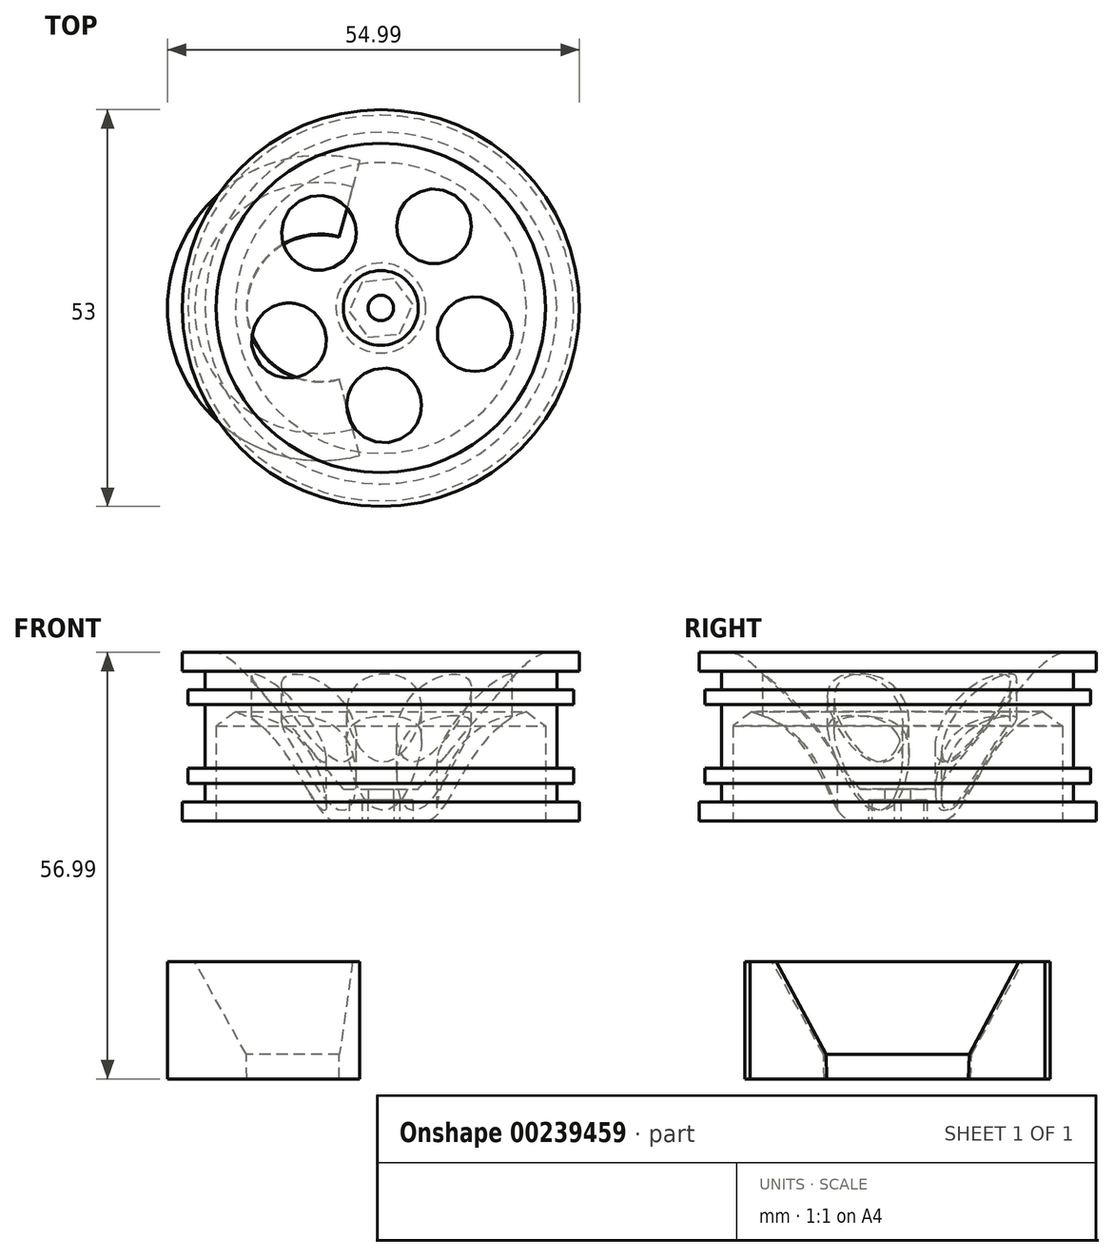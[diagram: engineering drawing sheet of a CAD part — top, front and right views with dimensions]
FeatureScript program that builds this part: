
annotation { "Feature Type Name" : "Feature", "Feature Type Description" : "" }
export const myFeature = defineFeature(function(context is Context, id is Id, definition is map)
    precondition{}
    {
        {
            var Q0;
            Q0=qCreatedBy(makeId("Front.planeOp"),FACE);
            var sketch = newSketch(context, id + "F0", { "sketchPlane" : qUnion([Q0])});
            skLineSegment(sketch, "E0", {"start": v(-30.1, -5.77) * mm, "end": v(-34.6, -5.77) * mm});
            skLineSegment(sketch, "E1", {"start": v(-34.6, -5.77) * mm, "end": v(-34.6, -8.27) * mm});
            skLineSegment(sketch, "E2", {"start": v(-34.6, -8.27) * mm, "end": v(-31.6, -8.27) * mm});
            skLineSegment(sketch, "E3", {"start": v(-31.6, -8.27) * mm, "end": v(-31.6, -10.77) * mm});
            skLineSegment(sketch, "E4", {"start": v(-31.6, -10.77) * mm, "end": v(-33.84, -10.77) * mm});
            skLineSegment(sketch, "E5", {"start": v(-33.84, -10.77) * mm, "end": v(-33.84, -12.77) * mm});
            skLineSegment(sketch, "E6", {"start": v(-33.84, -12.77) * mm, "end": v(-31.6, -12.77) * mm});
            skLineSegment(sketch, "E7", {"start": v(-31.6, -12.77) * mm, "end": v(-31.6, -21.27) * mm});
            skLineSegment(sketch, "E8", {"start": v(-31.6, -21.27) * mm, "end": v(-33.84, -21.27) * mm});
            skLineSegment(sketch, "E9", {"start": v(-33.84, -21.27) * mm, "end": v(-33.84, -23.27) * mm});
            skLineSegment(sketch, "E10", {"start": v(-33.84, -23.27) * mm, "end": v(-31.6, -23.27) * mm});
            skLineSegment(sketch, "E11", {"start": v(-31.6, -23.27) * mm, "end": v(-31.6, -25.77) * mm});
            skLineSegment(sketch, "E12", {"start": v(-31.6, -25.77) * mm, "end": v(-34.6, -25.77) * mm});
            skLineSegment(sketch, "E13", {"start": v(-34.6, -25.77) * mm, "end": v(-34.6, -28.27) * mm});
            skLineSegment(sketch, "E14", {"start": v(-34.6, -28.27) * mm, "end": v(-30.1, -28.27) * mm});
            skLineSegment(sketch, "E15", {"start": v(-14.1, -28.27) * mm, "end": v(-9.8, -28.27) * mm});
            skLineSegment(sketch, "E16", {"start": v(-9.8, -28.27) * mm, "end": v(-9.8, -24.02) * mm});
            skLineSegment(sketch, "E17", {"start": v(-9.8, -24.02) * mm, "end": v(-13.1, -24.02) * mm});
            skLineSegment(sketch, "E18", {"start": v(-9.8, -28.27) * mm, "end": v(-8.1, -28.27) * mm});
            skLineSegment(sketch, "E19", {"start": v(-8.1, -28.27) * mm, "end": v(-8.1, -24.02) * mm});
            skLineSegment(sketch, "E20", {"start": v(-8.1, -24.02) * mm, "end": v(-9.8, -24.02) * mm});
            skLineSegment(sketch, "E21", {"start": v(-30.1, -28.27) * mm, "end": v(-30.1, -15.63) * mm});
            skFitSpline(sketch, "E22", {"points": [v(-30.1, -13.27) * mm, v(-25.48, -14.59) * mm, v(-19.31, -21.6) * mm, v(-14.1, -28.27) * mm], "startDerivative": vector(14.77, -0.8) * mm, "endDerivative": vector(13.28, 1.86) * mm});
            skLineSegment(sketch, "E23", {"start": v(-30.1, -15.63) * mm, "end": v(-27.52, -13.71) * mm});
            skFitSpline(sketch, "E24", {"points": [v(-13.1, -24.02) * mm, v(-16.9, -19.47) * mm, v(-23.9, -11.2) * mm, v(-30.1, -5.77) * mm], "startDerivative": vector(-12.08, 13.61) * mm, "endDerivative": vector(-19.93, 6.13) * mm});
            skSolve(sketch);
        }
        {
            var Q0;
            Q0=makeQuery(id+"F0.imprint","IMPRINT",FACE,{"disambiguationData":[TD([[makeQuery(id+"F0.imprint","IMPRINT",EDGE,{"derivedFrom":sQuery(id+"F0.wireOp",EDGE,"E0")}),1.0]])]});
            var Q1;
            Q1=sQuery(id+"F0.wireOp",EDGE,"E19");
            revolve(context, id + "F1", {"entities" : qUnion([Q0]), "axis" : qUnion([Q1]), "revolveType" : RevolveType.FULL});
        }
        {
            var Q0;
            Q0=makeQuery(id+"F1.opRevolve","SWEPT_BODY",BODY,{"disambiguationData":[OSD([sQuery(id+"F0.wireOp",EDGE,"E0"),sQuery(id+"F0.wireOp",EDGE,"E1"),sQuery(id+"F0.wireOp",EDGE,"E2"),sQuery(id+"F0.wireOp",EDGE,"E3"),sQuery(id+"F0.wireOp",EDGE,"E4"),sQuery(id+"F0.wireOp",EDGE,"E5"),sQuery(id+"F0.wireOp",EDGE,"E6"),sQuery(id+"F0.wireOp",EDGE,"E7"),sQuery(id+"F0.wireOp",EDGE,"E8"),sQuery(id+"F0.wireOp",EDGE,"E9"),sQuery(id+"F0.wireOp",EDGE,"E10"),sQuery(id+"F0.wireOp",EDGE,"E11"),sQuery(id+"F0.wireOp",EDGE,"E12"),sQuery(id+"F0.wireOp",EDGE,"E13"),sQuery(id+"F0.wireOp",EDGE,"E14"),sQuery(id+"F0.wireOp",EDGE,"E15"),sQuery(id+"F0.wireOp",EDGE,"E16"),sQuery(id+"F0.wireOp",EDGE,"E17"),sQuery(id+"F0.wireOp",EDGE,"d1fe35fa-0e64-46eb-b905-4f6e5b59d955"),sQuery(id+"F0.wireOp",EDGE,"E21"),sQuery(id+"F0.wireOp",EDGE,"E22"),sQuery(id+"F0.wireOp",EDGE,"128adb2e-220a-4990-bb0a-539939f27e0b.filletArc")])]});
            transform(context, id + "F2", {"entities" : qUnion([Q0]), "transformType" : TransformType.TRANSLATION_3D, "dx" : 8.1 * mm, "dy" : 0 * mm, "dz" : 0 * mm, "makeCopy" : false});
        }
        {
            var Q0;
            Q0=qCreatedBy(makeId("Top.planeOp"),FACE);
            var sketch = newSketch(context, id + "F3", { "sketchPlane" : qUnion([Q0])});
            skCircle(sketch, "E25", {"center": v(-8.27, 10.04) * mm, "radius": 5 * mm});
            skCircle(sketch, "E26.1.0", {"center": v(7.1, 10.9) * mm, "radius": 5 * mm});
            skCircle(sketch, "E26.2.0", {"center": v(12.53, -3.49) * mm, "radius": 5 * mm});
            skCircle(sketch, "E26.3.0", {"center": v(0.44, -13) * mm, "radius": 5 * mm});
            skCircle(sketch, "E26.4.0", {"center": v(-12.27, -4.33) * mm, "radius": 5 * mm});
            skPoint(sketch, "E26.center", {"position": v(0, 0) * mm});
            skLineSegment(sketch, "E26.anchor1", {"start": v(0, 0) * mm, "end": v(-8.27, 10.04) * mm, "construction": true});
            skLineSegment(sketch, "E26.anchor2", {"start": v(0, 0) * mm, "end": v(-12.27, -4.33) * mm, "construction": true});
            skSolve(sketch);
        }
        {
            var Q0;
            Q0=makeQuery(id+"F3.imprint","IMPRINT",FACE,{"disambiguationData":[TD([[makeQuery(id+"F3.imprint","IMPRINT",EDGE,{"derivedFrom":sQuery(id+"F3.wireOp",EDGE,"E25")}),1.0]])]});
            var Q1;
            Q1=makeQuery(id+"F3.imprint","IMPRINT",FACE,{"disambiguationData":[TD([[makeQuery(id+"F3.imprint","IMPRINT",EDGE,{"derivedFrom":sQuery(id+"F3.wireOp",EDGE,"E26.1.0")}),1.0]])]});
            var Q2;
            Q2=makeQuery(id+"F3.imprint","IMPRINT",FACE,{"disambiguationData":[TD([[makeQuery(id+"F3.imprint","IMPRINT",EDGE,{"derivedFrom":sQuery(id+"F3.wireOp",EDGE,"E26.2.0")}),1.0]])]});
            var Q3;
            Q3=makeQuery(id+"F3.imprint","IMPRINT",FACE,{"disambiguationData":[TD([[makeQuery(id+"F3.imprint","IMPRINT",EDGE,{"derivedFrom":sQuery(id+"F3.wireOp",EDGE,"E26.3.0")}),1.0]])]});
            var Q4;
            Q4=makeQuery(id+"F3.imprint","IMPRINT",FACE,{"disambiguationData":[TD([[makeQuery(id+"F3.imprint","IMPRINT",EDGE,{"derivedFrom":sQuery(id+"F3.wireOp",EDGE,"E26.4.0")}),1.0]])]});
            var Q5;
            Q5=sQuery(id+"F3.wireOp",EDGE,"E25");
            var Q6;
            Q6=sQuery(id+"F3.wireOp",EDGE,"E26.1.0");
            var Q7;
            Q7=sQuery(id+"F3.wireOp",EDGE,"E26.2.0");
            var Q8;
            Q8=sQuery(id+"F3.wireOp",EDGE,"E26.3.0");
            var Q9;
            Q9=sQuery(id+"F3.wireOp",EDGE,"E26.4.0");
            extrude(context, id + "F4", {"entities" : qUnion([Q0, Q1, Q2, Q3, Q4]), "operationType" : NewBodyOperationType.REMOVE, "surfaceEntities" : qUnion([Q5, Q6, Q7, Q8, Q9]), "endBound" : BoundingType.THROUGH_ALL, "oppositeDirection" : true, "depth" : 25 * mm});
        }
        {
            var Q0;
            Q0=makeQuery(id+"F1.opRevolve","SWEPT_BODY",BODY,{"disambiguationData":[OSD([sQuery(id+"F0.wireOp",EDGE,"E0"),sQuery(id+"F0.wireOp",EDGE,"E1"),sQuery(id+"F0.wireOp",EDGE,"E2"),sQuery(id+"F0.wireOp",EDGE,"E3"),sQuery(id+"F0.wireOp",EDGE,"E4"),sQuery(id+"F0.wireOp",EDGE,"E5"),sQuery(id+"F0.wireOp",EDGE,"E6"),sQuery(id+"F0.wireOp",EDGE,"E7"),sQuery(id+"F0.wireOp",EDGE,"E8"),sQuery(id+"F0.wireOp",EDGE,"E9"),sQuery(id+"F0.wireOp",EDGE,"E10"),sQuery(id+"F0.wireOp",EDGE,"E11"),sQuery(id+"F0.wireOp",EDGE,"E12"),sQuery(id+"F0.wireOp",EDGE,"E13"),sQuery(id+"F0.wireOp",EDGE,"E14"),sQuery(id+"F0.wireOp",EDGE,"E15"),sQuery(id+"F0.wireOp",EDGE,"E16"),sQuery(id+"F0.wireOp",EDGE,"E17"),sQuery(id+"F0.wireOp",EDGE,"d1fe35fa-0e64-46eb-b905-4f6e5b59d955"),sQuery(id+"F0.wireOp",EDGE,"E21"),sQuery(id+"F0.wireOp",EDGE,"E22"),sQuery(id+"F0.wireOp",EDGE,"128adb2e-220a-4990-bb0a-539939f27e0b.filletArc")])]});
            transform(context, id + "F5", {"entities" : qUnion([Q0]), "transformType" : TransformType.TRANSLATION_3D, "dx" : 0 * mm, "dy" : 0 * mm, "dz" : 30 * mm, "makeCopy" : false});
        }
        {
            var Q0;
            Q0=qCreatedBy(makeId("Top.planeOp"),FACE);
            var sketch = newSketch(context, id + "F6", { "sketchPlane" : qUnion([Q0])});
            skCircle(sketch, "E27.cCircle", {"center": v(0, 0) * mm, "radius": 3.7 * mm, "construction": true});
            skLineSegment(sketch, "E27.0", {"start": v(1.73, 3.9) * mm, "end": v(4.25, 0.46) * mm});
            skLineSegment(sketch, "E27.1", {"start": v(4.25, 0.46) * mm, "end": v(2.52, -3.45) * mm});
            skLineSegment(sketch, "E27.2", {"start": v(2.52, -3.45) * mm, "end": v(-1.73, -3.9) * mm});
            skLineSegment(sketch, "E27.3", {"start": v(-1.73, -3.9) * mm, "end": v(-4.25, -0.46) * mm});
            skLineSegment(sketch, "E27.4", {"start": v(-4.25, -0.46) * mm, "end": v(-2.52, 3.45) * mm});
            skLineSegment(sketch, "E27.5", {"start": v(-2.52, 3.45) * mm, "end": v(1.73, 3.9) * mm});
            skPoint(sketch, "E27.0.midPoint", {"position": v(2.99, 2.18) * mm});
            skSolve(sketch);
        }
        {
            var Q0;
            Q0=makeQuery(id+"F6.imprint","IMPRINT",FACE,{"disambiguationData":[TD([[makeQuery(id+"F6.imprint","IMPRINT",EDGE,{"derivedFrom":sQuery(id+"F6.wireOp",EDGE,"E27.0")}),-1.0]])]});
            extrude(context, id + "F7", {"entities" : qUnion([Q0]), "operationType" : NewBodyOperationType.REMOVE, "depth" : 4.5 * mm});
        }
        {
            var Q0;
            Q0=qCreatedBy(makeId("Front.planeOp"),FACE);
            var sketch = newSketch(context, id + "F8", { "sketchPlane" : qUnion([Q0])});
            skLineSegment(sketch, "E28", {"start": v(-28.49, -17.09) * mm, "end": v(-28.49, -32.76) * mm});
            skLineSegment(sketch, "E29", {"start": v(-28.49, -32.76) * mm, "end": v(-17.88, -32.76) * mm});
            skLineSegment(sketch, "E30", {"start": v(-17.88, -32.76) * mm, "end": v(-17.98, -29.51) * mm});
            skLineSegment(sketch, "E31", {"start": v(-28.49, -17.09) * mm, "end": v(-24.86, -17.09) * mm});
            skLineSegment(sketch, "E32", {"start": v(-24.86, -17.09) * mm, "end": v(-17.98, -29.51) * mm});
            skSolve(sketch);
        }
        {
            var Q0;
            Q0=makeQuery(id+"F8.imprint","IMPRINT",FACE,{"disambiguationData":[TD([[makeQuery(id+"F8.imprint","IMPRINT",EDGE,{"derivedFrom":sQuery(id+"F8.wireOp",EDGE,"E28")}),1.0]])]});
            var Q1;
            Q1=sQuery(id+"F0.wireOp",EDGE,"E19");
            revolve(context, id + "F9", {"entities" : qUnion([Q0]), "axis" : qUnion([Q1]), "revolveType" : RevolveType.SYMMETRIC, "angle" : 210 * degree});
        }
    });
